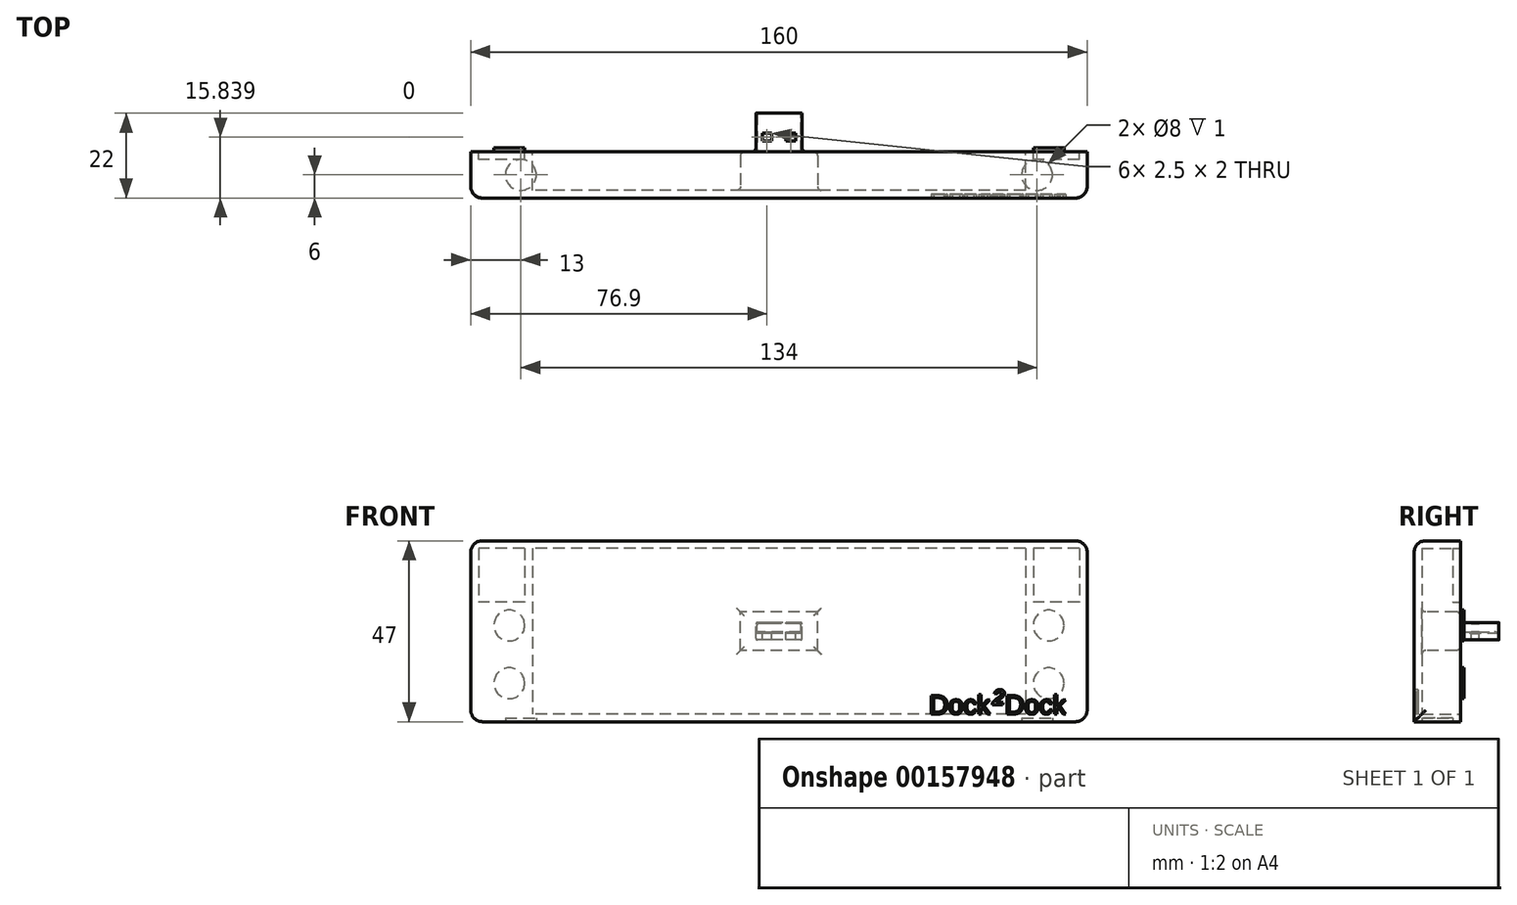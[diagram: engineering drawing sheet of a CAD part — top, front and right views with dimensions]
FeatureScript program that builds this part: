
annotation { "Feature Type Name" : "Feature", "Feature Type Description" : "" }
export const myFeature = defineFeature(function(context is Context, id is Id, definition is map)
    precondition{}
    {
        {
            var Q0;
            Q0=qCreatedBy(makeId("Right.planeOp"),FACE);
            var sketch = newSketch(context, id + "F0", { "sketchPlane" : qUnion([Q0])});
            skLineSegment(sketch, "E0.top", {"start": v(-6, -23.5) * mm, "end": v(6, -23.5) * mm});
            skLineSegment(sketch, "E0.left", {"start": v(-6, 23.5) * mm, "end": v(-6, -23.5) * mm});
            skLineSegment(sketch, "E0.right", {"start": v(6, 23.5) * mm, "end": v(6, -23.5) * mm});
            skPoint(sketch, "E0.middle", {"position": v(0, 0) * mm});
            skLineSegment(sketch, "E1.bottom", {"start": v(-6, 23.5) * mm, "end": v(6, 23.5) * mm});
            skLineSegment(sketch, "E1.left", {"start": v(-6, 23.5) * mm, "end": v(-6, 19.5) * mm});
            skLineSegment(sketch, "E1.right", {"start": v(6, 23.5) * mm, "end": v(6, 19.5) * mm});
            skSolve(sketch);
        }
        {
            var Q0;
            {var subQ1=sQuery(id+"F0.wireOp",EDGE,"E0.top");Q0=makeQuery(id+"F0.imprint","IMPRINT",FACE,{"disambiguationData":[TD([[makeQuery(id+"F0.imprint","IMPRINT",EDGE,{"derivedFrom":subQ1}),1.0]])]});}
            var Q1;
            {var subQ1=sQuery(id+"F0.wireOp",EDGE,"E0.top");Q1=makeQuery(id+"F0.imprint","IMPRINT",FACE,{"disambiguationData":[TD([[makeQuery(id+"F0.imprint","IMPRINT",EDGE,{"derivedFrom":subQ1}),1.0]])]});}
            extrude(context, id + "F1", {"entities" : qUnion([Q0, Q1]), "endBound" : BoundingType.SYMMETRIC, "depth" : 160 * mm});
        }
        {
            var Q0;
            Q0=makeQuery(id+"F1.opExtrude","SWEPT_FACE",FACE,{"disambiguationData":[OSD([sQuery(id+"F0.wireOp",EDGE,"E0.right")])]});
            var sketch = newSketch(context, id + "F2", { "sketchPlane" : qUnion([Q0])});
            skPoint(sketch, "E2.middle", {"position": v(0, 0) * mm});
            skLineSegment(sketch, "E3.bottom", {"start": v(70, 1.5) * mm, "end": v(-70, 1.5) * mm});
            skLineSegment(sketch, "E3.top", {"start": v(70, -13.5) * mm, "end": v(-70, -13.5) * mm});
            skLineSegment(sketch, "E3.left", {"start": v(70, 1.5) * mm, "end": v(70, -13.5) * mm});
            skLineSegment(sketch, "E3.right", {"start": v(-70, 1.5) * mm, "end": v(-70, -13.5) * mm});
            skCircle(sketch, "E4", {"center": v(70, 1.5) * mm, "radius": 4 * mm});
            skCircle(sketch, "E5", {"center": v(-70, 1.5) * mm, "radius": 4 * mm});
            skCircle(sketch, "E6", {"center": v(70, -13.5) * mm, "radius": 4 * mm});
            skCircle(sketch, "E7", {"center": v(-70, -13.5) * mm, "radius": 4 * mm});
            skSolve(sketch);
        }
        {
            var Q0;
            {var subQ0=sQuery(id+"F2.wireOp",EDGE,"E3.right");var subQ1=sQuery(id+"F2.wireOp",EDGE,"E3.top");var subQ2=makeQuery(id+"F2.imprint","INTERSECT",VERTEX,{"derivedFrom":[subQ1,subQ0]});Q0=makeQuery(id+"F2.imprint","IMPRINT",FACE,{"disambiguationData":[TD([[makeQuery(id+"F2.imprint","IMPRINT",EDGE,{"disambiguationData":[TD([[subQ2,1.0]])],"derivedFrom":subQ1}),1.0]])]});}
            var Q1;
            {var subQ0=sQuery(id+"F2.wireOp",EDGE,"E3.right");var subQ1=sQuery(id+"F2.wireOp",EDGE,"E3.top");var subQ2=makeQuery(id+"F2.imprint","INTERSECT",VERTEX,{"derivedFrom":[subQ1,subQ0]});Q1=makeQuery(id+"F2.imprint","IMPRINT",FACE,{"disambiguationData":[TD([[makeQuery(id+"F2.imprint","IMPRINT",EDGE,{"disambiguationData":[TD([[subQ2,1.0]])],"derivedFrom":subQ1}),-1.0]])]});}
            var Q2;
            {var subQ0=sQuery(id+"F2.wireOp",EDGE,"E3.right");var subQ1=sQuery(id+"F2.wireOp",EDGE,"E3.bottom");var subQ2=makeQuery(id+"F2.imprint","INTERSECT",VERTEX,{"derivedFrom":[subQ1,subQ0]});Q2=makeQuery(id+"F2.imprint","IMPRINT",FACE,{"disambiguationData":[TD([[makeQuery(id+"F2.imprint","IMPRINT",EDGE,{"disambiguationData":[TD([[subQ2,1.0]])],"derivedFrom":subQ1}),1.0]])]});}
            var Q3;
            {var subQ0=sQuery(id+"F2.wireOp",EDGE,"E3.right");var subQ1=sQuery(id+"F2.wireOp",EDGE,"E3.bottom");var subQ2=makeQuery(id+"F2.imprint","INTERSECT",VERTEX,{"derivedFrom":[subQ1,subQ0]});Q3=makeQuery(id+"F2.imprint","IMPRINT",FACE,{"disambiguationData":[TD([[makeQuery(id+"F2.imprint","IMPRINT",EDGE,{"disambiguationData":[TD([[subQ2,1.0]])],"derivedFrom":subQ1}),-1.0]])]});}
            var Q4;
            {var subQ0=sQuery(id+"F2.wireOp",EDGE,"E3.left");var subQ1=sQuery(id+"F2.wireOp",EDGE,"E3.top");var subQ2=makeQuery(id+"F2.imprint","INTERSECT",VERTEX,{"derivedFrom":[subQ1,subQ0]});Q4=makeQuery(id+"F2.imprint","IMPRINT",FACE,{"disambiguationData":[TD([[makeQuery(id+"F2.imprint","IMPRINT",EDGE,{"disambiguationData":[TD([[subQ2,-1.0]])],"derivedFrom":subQ1}),-1.0]])]});}
            var Q5;
            {var subQ0=sQuery(id+"F2.wireOp",EDGE,"E3.left");var subQ1=sQuery(id+"F2.wireOp",EDGE,"E3.top");var subQ2=makeQuery(id+"F2.imprint","INTERSECT",VERTEX,{"derivedFrom":[subQ1,subQ0]});Q5=makeQuery(id+"F2.imprint","IMPRINT",FACE,{"disambiguationData":[TD([[makeQuery(id+"F2.imprint","IMPRINT",EDGE,{"disambiguationData":[TD([[subQ2,-1.0]])],"derivedFrom":subQ1}),1.0]])]});}
            var Q6;
            {var subQ0=sQuery(id+"F2.wireOp",EDGE,"E3.left");var subQ1=sQuery(id+"F2.wireOp",EDGE,"E3.bottom");var subQ2=makeQuery(id+"F2.imprint","INTERSECT",VERTEX,{"derivedFrom":[subQ1,subQ0]});Q6=makeQuery(id+"F2.imprint","IMPRINT",FACE,{"disambiguationData":[TD([[makeQuery(id+"F2.imprint","IMPRINT",EDGE,{"disambiguationData":[TD([[subQ2,-1.0]])],"derivedFrom":subQ1}),-1.0]])]});}
            var Q7;
            {var subQ0=sQuery(id+"F2.wireOp",EDGE,"E3.left");var subQ1=sQuery(id+"F2.wireOp",EDGE,"E3.bottom");var subQ2=makeQuery(id+"F2.imprint","INTERSECT",VERTEX,{"derivedFrom":[subQ1,subQ0]});Q7=makeQuery(id+"F2.imprint","IMPRINT",FACE,{"disambiguationData":[TD([[makeQuery(id+"F2.imprint","IMPRINT",EDGE,{"disambiguationData":[TD([[subQ2,-1.0]])],"derivedFrom":subQ1}),1.0]])]});}
            var Q8;
            Q8=sQuery(id+"F2.wireOp",EDGE,"E5");
            extrude(context, id + "F3", {"entities" : qUnion([Q0, Q1, Q2, Q3, Q4, Q5, Q6, Q7]), "operationType" : NewBodyOperationType.ADD, "surfaceEntities" : qUnion([Q8]), "depth" : 1 * mm});
        }
        {
            var Q0;
            {var subQ0=sQuery(id+"F0.wireOp",EDGE,"E0.right");Q0=makeQuery(id+"F2.imprint","IMPRINT",FACE,{"disambiguationData":[TD([[makeQuery(id+"F2.imprint","IMPRINT",EDGE,{"derivedFrom":makeQuery(id+"F1.opExtrude","CAP_EDGE",EDGE,{"disambiguationData":[OSD([subQ0])],"isStart":true})}),-1.0]])]});}
            var sketch = newSketch(context, id + "F4", { "sketchPlane" : qUnion([Q0])});
            skLineSegment(sketch, "E8.bottom", {"start": v(-64, 21.5) * mm, "end": v(64, 21.5) * mm});
            skLineSegment(sketch, "E8.top", {"start": v(-64, -21.5) * mm, "end": v(64, -21.5) * mm});
            skLineSegment(sketch, "E8.left", {"start": v(-64, 21.5) * mm, "end": v(-64, -21.5) * mm});
            skLineSegment(sketch, "E8.right", {"start": v(64, 21.5) * mm, "end": v(64, -21.5) * mm});
            skPoint(sketch, "E8.middle", {"position": v(0, 0) * mm});
            skSolve(sketch);
        }
        {
            var Q0;
            Q0=qSketchRegion(id+"F4",true);
            extrude(context, id + "F5", {"entities" : qUnion([Q0]), "operationType" : NewBodyOperationType.REMOVE, "oppositeDirection" : true, "depth" : 10 * mm});
        }
        {
            var Q0;
            Q0=makeQuery(id+"F1.opExtrude","SWEPT_FACE",FACE,{"disambiguationData":[OSD([sQuery(id+"F0.wireOp",EDGE,"E0.top")])]});
            var sketch = newSketch(context, id + "F6", { "sketchPlane" : qUnion([Q0])});
            skCircle(sketch, "E9", {"center": v(67, 0) * mm, "radius": 4 * mm});
            skCircle(sketch, "E10", {"center": v(-67, 0) * mm, "radius": 4 * mm});
            skSolve(sketch);
        }
        {
            var Q0;
            Q0=qSketchRegion(id+"F6",true);
            extrude(context, id + "F7", {"entities" : qUnion([Q0]), "operationType" : NewBodyOperationType.REMOVE, "oppositeDirection" : true, "depth" : 1 * mm});
        }
        {
            var Q0;
            Q0=makeQuery(id+"F1.opExtrude","SWEPT_EDGE",EDGE,{"disambiguationData":[OSD([sQuery(id+"F0.wireOp",EDGE,"E0.left"),sQuery(id+"F0.wireOp",EDGE,"E1.bottom")])]});
            fillet(context, id + "F8", {"entities" : qUnion([Q0]), "radius" : 3 * mm, "tangentPropagation" : true, "allowEdgeOverflow" : false});
        }
        {
            var Q0;
            Q0=makeQuery(id+"F1.opExtrude","SWEPT_FACE",FACE,{"disambiguationData":[OSD([sQuery(id+"F0.wireOp",EDGE,"E0.left")])]});
            var sketch = newSketch(context, id + "F9", { "sketchPlane" : qUnion([Q0])});
            skText(sketch, "E11", { "text": "Dock  Dock", "fontName": "Arimo-Regular.ttf"});
            skText(sketch, "E12", { "text": "2", "fontName": "Arimo-BoldItalic.ttf"});
            const initialGuessF9  = {"E11": [0.039, -0.0215, 1, 0, 0.005], "E12": [0.05543, -0.01913, 1, 0, 0.0041]};
            skSetInitialGuess(sketch, initialGuessF9);
            skSolve(sketch);
        }
        {
            var Q0;
            Q0=qSketchRegion(id+"F9",true);
            extrude(context, id + "F10", {"entities" : qUnion([Q0]), "operationType" : NewBodyOperationType.REMOVE, "oppositeDirection" : true, "depth" : 1 * mm});
        }
        {
            var Q0;
            Q0=makeQuery(id+"F1.opExtrude","CAP_EDGE",EDGE,{"disambiguationData":[OSD([sQuery(id+"F0.wireOp",EDGE,"E1.bottom")])],"isStart":true});
            var Q1;
            {var subQ0=sQuery(id+"F0.wireOp",EDGE,"E1.bottom");var subQ1=sQuery(id+"F0.wireOp",EDGE,"E0.left");Q1=makeQuery(id+"F8.opFillet","BLEND_EDGE",EDGE,{"blendedFrom":[makeQuery(id+"F1.opExtrude","SWEPT_EDGE",EDGE,{"disambiguationData":[OSD([subQ1,subQ0])]}),makeQuery(id+"F1.opExtrude","CAP_FACE",FACE,{"disambiguationData":[OSD([sQuery(id+"F0.wireOp",EDGE,"E0.top"),subQ1,sQuery(id+"F0.wireOp",EDGE,"E0.right"),subQ0])],"isStart":true})],"blendedInto":[makeQuery(id+"F1.opExtrude","CAP_FACE",FACE,{"disambiguationData":[OSD([sQuery(id+"F0.wireOp",EDGE,"E0.top"),subQ1,sQuery(id+"F0.wireOp",EDGE,"E0.right"),subQ0])],"isStart":true})]});}
            var Q2;
            Q2=makeQuery(id+"F1.opExtrude","CAP_EDGE",EDGE,{"disambiguationData":[OSD([sQuery(id+"F0.wireOp",EDGE,"E0.left")])],"isStart":true});
            var Q3;
            Q3=makeQuery(id+"F1.opExtrude","CAP_EDGE",EDGE,{"disambiguationData":[OSD([sQuery(id+"F0.wireOp",EDGE,"E0.left")])],"isStart":false});
            var Q4;
            {var subQ0=sQuery(id+"F0.wireOp",EDGE,"E1.bottom");var subQ1=sQuery(id+"F0.wireOp",EDGE,"E0.left");Q4=makeQuery(id+"F8.opFillet","BLEND_EDGE",EDGE,{"blendedFrom":[makeQuery(id+"F1.opExtrude","SWEPT_EDGE",EDGE,{"disambiguationData":[OSD([subQ1,subQ0])]}),makeQuery(id+"F1.opExtrude","CAP_FACE",FACE,{"disambiguationData":[OSD([sQuery(id+"F0.wireOp",EDGE,"E0.top"),subQ1,sQuery(id+"F0.wireOp",EDGE,"E0.right"),subQ0])],"isStart":false})],"blendedInto":[makeQuery(id+"F1.opExtrude","CAP_FACE",FACE,{"disambiguationData":[OSD([sQuery(id+"F0.wireOp",EDGE,"E0.top"),subQ1,sQuery(id+"F0.wireOp",EDGE,"E0.right"),subQ0])],"isStart":false})]});}
            var Q5;
            Q5=makeQuery(id+"F1.opExtrude","CAP_EDGE",EDGE,{"disambiguationData":[OSD([sQuery(id+"F0.wireOp",EDGE,"E1.bottom")])],"isStart":false});
            var Q6;
            Q6=makeQuery(id+"F1.opExtrude","CAP_EDGE",EDGE,{"disambiguationData":[OSD([sQuery(id+"F0.wireOp",EDGE,"E0.top")])],"isStart":false});
            var Q7;
            Q7=makeQuery(id+"F1.opExtrude","CAP_EDGE",EDGE,{"disambiguationData":[OSD([sQuery(id+"F0.wireOp",EDGE,"E0.top")])],"isStart":true});
            fillet(context, id + "F11", {"entities" : qUnion([Q0, Q1, Q2, Q3, Q4, Q5, Q6, Q7]), "radius" : 3 * mm, "tangentPropagation" : true, "allowEdgeOverflow" : false});
        }
        {
            var Q0;
            {var subQ0=sQuery(id+"F0.wireOp",EDGE,"E0.right");Q0=makeQuery(id+"F2.imprint","IMPRINT",FACE,{"disambiguationData":[TD([[makeQuery(id+"F2.imprint","IMPRINT",EDGE,{"derivedFrom":makeQuery(id+"F1.opExtrude","CAP_EDGE",EDGE,{"disambiguationData":[OSD([subQ0])],"isStart":true})}),-1.0]])]});}
            var sketch = newSketch(context, id + "F12", { "sketchPlane" : qUnion([Q0])});
            skLineSegment(sketch, "E13.bottom", {"start": v(-78, 21.5) * mm, "end": v(-66, 21.5) * mm});
            skLineSegment(sketch, "E13.top", {"start": v(-78, 7.5) * mm, "end": v(-66, 7.5) * mm});
            skLineSegment(sketch, "E13.left", {"start": v(-78, 21.5) * mm, "end": v(-78, 7.5) * mm});
            skLineSegment(sketch, "E13.right", {"start": v(-66, 21.5) * mm, "end": v(-66, 7.5) * mm});
            skLineSegment(sketch, "E14.bottom", {"start": v(66, 21.5) * mm, "end": v(78, 21.5) * mm});
            skLineSegment(sketch, "E14.top", {"start": v(66, 7.5) * mm, "end": v(78, 7.5) * mm});
            skLineSegment(sketch, "E14.left", {"start": v(66, 21.5) * mm, "end": v(66, 7.5) * mm});
            skLineSegment(sketch, "E14.right", {"start": v(78, 21.5) * mm, "end": v(78, 7.5) * mm});
            skSolve(sketch);
        }
        {
            var Q0;
            Q0=qSketchRegion(id+"F12",true);
            extrude(context, id + "F13", {"entities" : qUnion([Q0]), "operationType" : NewBodyOperationType.REMOVE, "oppositeDirection" : true, "depth" : 2 * mm});
        }
        {
            var Q0;
            {var subQ2=sQuery(id+"F0.wireOp",EDGE,"E0.left");var subQ3=sQuery(id+"F0.wireOp",EDGE,"E0.top");Q0=makeQuery(id+"F10.boolean.opBoolean","SPLIT",FACE,{"disambiguationData":[TD([makeQuery(id+"F1.opExtrude","SWEPT_FACE",FACE,{"disambiguationData":[OSD([subQ3])]})])],"derivedFrom":makeQuery(id+"F1.opExtrude","SWEPT_FACE",FACE,{"disambiguationData":[OSD([subQ2])]})});}
            var sketch = newSketch(context, id + "F14", { "sketchPlane" : qUnion([Q0])});
            skLineSegment(sketch, "E15.bottom", {"start": v(-10, 5) * mm, "end": v(10, 5) * mm});
            skLineSegment(sketch, "E15.top", {"start": v(-10, -5) * mm, "end": v(10, -5) * mm});
            skLineSegment(sketch, "E15.left", {"start": v(-10, 5) * mm, "end": v(-10, -5) * mm});
            skLineSegment(sketch, "E15.right", {"start": v(10, 5) * mm, "end": v(10, -5) * mm});
            skSolve(sketch);
        }
        {
            var Q0;
            Q0=qSketchRegion(id+"F14",true);
            extrude(context, id + "F15", {"entities" : qUnion([Q0]), "operationType" : NewBodyOperationType.ADD, "oppositeDirection" : true, "depth" : 12 * mm});
        }
        {
            var Q0;
            Q0=makeQuery(id+"F15.opExtrude","CAP_FACE",FACE,{"disambiguationData":[OSD([sQuery(id+"F14.wireOp",EDGE,"E15.bottom"),sQuery(id+"F14.wireOp",EDGE,"E15.top"),sQuery(id+"F14.wireOp",EDGE,"E15.left"),sQuery(id+"F14.wireOp",EDGE,"E15.right")])],"isStart":false});
            var sketch = newSketch(context, id + "F16", { "sketchPlane" : qUnion([Q0])});
            skLineSegment(sketch, "E16.bottom", {"start": v(-6, -2.25) * mm, "end": v(6, -2.25) * mm});
            skLineSegment(sketch, "E16.top", {"start": v(-6, 2.25) * mm, "end": v(6, 2.25) * mm});
            skLineSegment(sketch, "E16.left", {"start": v(-6, -2.25) * mm, "end": v(-6, 2.25) * mm});
            skLineSegment(sketch, "E16.right", {"start": v(6, -2.25) * mm, "end": v(6, 2.25) * mm});
            skPoint(sketch, "E16.middle", {"position": v(0, 0) * mm});
            skLineSegment(sketch, "E17.bottom", {"start": v(-5.7, -0.6) * mm, "end": v(5.7, -0.6) * mm});
            skLineSegment(sketch, "E17.top", {"start": v(-5.7, 1.95) * mm, "end": v(5.7, 1.95) * mm});
            skLineSegment(sketch, "E17.left", {"start": v(-5.7, -0.6) * mm, "end": v(-5.7, 1.95) * mm});
            skLineSegment(sketch, "E17.right", {"start": v(5.7, -0.6) * mm, "end": v(5.7, 1.95) * mm});
            skSolve(sketch);
        }
        {
            var Q0;
            Q0=qSketchRegion(id+"F16",true);
            extrude(context, id + "F17", {"entities" : qUnion([Q0]), "operationType" : NewBodyOperationType.ADD, "depth" : 10 * mm});
        }
        {
            var Q0;
            Q0=makeQuery(id+"F17.opExtrude","SWEPT_EDGE",EDGE,{"disambiguationData":[OSD([sQuery(id+"F16.wireOp",EDGE,"E17.top"),sQuery(id+"F16.wireOp",EDGE,"E17.left")])]});
            var Q1;
            Q1=makeQuery(id+"F17.opExtrude","SWEPT_EDGE",EDGE,{"disambiguationData":[OSD([sQuery(id+"F16.wireOp",EDGE,"E17.top"),sQuery(id+"F16.wireOp",EDGE,"E17.right")])]});
            var Q2;
            Q2=makeQuery(id+"F17.opExtrude","SWEPT_EDGE",EDGE,{"disambiguationData":[OSD([sQuery(id+"F16.wireOp",EDGE,"E16.top"),sQuery(id+"F16.wireOp",EDGE,"E16.left")])]});
            var Q3;
            Q3=makeQuery(id+"F17.opExtrude","SWEPT_EDGE",EDGE,{"disambiguationData":[OSD([sQuery(id+"F16.wireOp",EDGE,"E16.bottom"),sQuery(id+"F16.wireOp",EDGE,"E16.left")])]});
            var Q4;
            Q4=makeQuery(id+"F17.opExtrude","SWEPT_EDGE",EDGE,{"disambiguationData":[OSD([sQuery(id+"F16.wireOp",EDGE,"E16.bottom"),sQuery(id+"F16.wireOp",EDGE,"E16.right")])]});
            var Q5;
            Q5=makeQuery(id+"F17.opExtrude","SWEPT_EDGE",EDGE,{"disambiguationData":[OSD([sQuery(id+"F16.wireOp",EDGE,"E16.top"),sQuery(id+"F16.wireOp",EDGE,"E16.right")])]});
            fillet(context, id + "F18", {"entities" : qUnion([Q0, Q1, Q2, Q3, Q4, Q5]), "radius" : 0.4 * mm, "tangentPropagation" : true, "allowEdgeOverflow" : false});
        }
        {
            var Q0;
            Q0=makeQuery(id+"F17.opExtrude","CAP_FACE",FACE,{"disambiguationData":[OSD([sQuery(id+"F16.wireOp",EDGE,"E16.bottom"),sQuery(id+"F16.wireOp",EDGE,"E16.top"),sQuery(id+"F16.wireOp",EDGE,"E16.left"),sQuery(id+"F16.wireOp",EDGE,"E16.right"),sQuery(id+"F16.wireOp",EDGE,"E17.bottom"),sQuery(id+"F16.wireOp",EDGE,"E17.top"),sQuery(id+"F16.wireOp",EDGE,"E17.left"),sQuery(id+"F16.wireOp",EDGE,"E17.right")])],"isStart":false});
            var sketch = newSketch(context, id + "F19", { "sketchPlane" : qUnion([Q0])});
            skLineSegment(sketch, "E18.bottom", {"start": v(-5.7, -0.6) * mm, "end": v(5.7, -0.6) * mm});
            skLineSegment(sketch, "E18.top", {"start": v(-5.7, -0.2) * mm, "end": v(5.7, -0.2) * mm});
            skLineSegment(sketch, "E18.left", {"start": v(-5.7, -0.6) * mm, "end": v(-5.7, -0.2) * mm});
            skLineSegment(sketch, "E18.right", {"start": v(5.7, -0.6) * mm, "end": v(5.7, -0.2) * mm});
            skSolve(sketch);
        }
        {
            var Q0;
            Q0=qSketchRegion(id+"F19",true);
            extrude(context, id + "F20", {"entities" : qUnion([Q0]), "oppositeDirection" : true, "depth" : 10 * mm});
        }
        {
            var Q0;
            Q0=makeQuery(id+"F20.opExtrude","CAP_EDGE",EDGE,{"disambiguationData":[OSD([sQuery(id+"F19.wireOp",EDGE,"E18.top")])],"isStart":true});
            fillet(context, id + "F21", {"entities" : qUnion([Q0]), "radius" : 2 * mm, "tangentPropagation" : true, "allowEdgeOverflow" : false});
        }
        {
            var Q0;
            Q0=makeQuery(id+"F17.opExtrude","SWEPT_FACE",FACE,{"disambiguationData":[OSD([sQuery(id+"F16.wireOp",EDGE,"E16.top")])]});
            var sketch = newSketch(context, id + "F22", { "sketchPlane" : qUnion([Q0])});
            skLineSegment(sketch, "E19.bottom", {"start": v(4.35, 8.84) * mm, "end": v(1.85, 8.84) * mm});
            skLineSegment(sketch, "E19.top", {"start": v(4.35, 10.84) * mm, "end": v(1.85, 10.84) * mm});
            skLineSegment(sketch, "E19.left", {"start": v(4.35, 8.84) * mm, "end": v(4.35, 10.84) * mm});
            skLineSegment(sketch, "E19.right", {"start": v(1.85, 8.84) * mm, "end": v(1.85, 10.84) * mm});
            skLineSegment(sketch, "E20.bottom", {"start": v(-1.85, 8.84) * mm, "end": v(-4.35, 8.84) * mm});
            skLineSegment(sketch, "E20.top", {"start": v(-1.85, 10.84) * mm, "end": v(-4.35, 10.84) * mm});
            skLineSegment(sketch, "E20.left", {"start": v(-1.85, 8.84) * mm, "end": v(-1.85, 10.84) * mm});
            skLineSegment(sketch, "E20.right", {"start": v(-4.35, 8.84) * mm, "end": v(-4.35, 10.84) * mm});
            skSolve(sketch);
        }
        {
            var Q0;
            Q0=qSketchRegion(id+"F22",true);
            extrude(context, id + "F23", {"entities" : qUnion([Q0]), "operationType" : NewBodyOperationType.REMOVE, "oppositeDirection" : true, "depth" : 5 * mm});
        }
        {
            var Q0;
            {var subQ0=sQuery(id+"F14.wireOp",EDGE,"E15.left");var subQ1=sQuery(id+"F14.wireOp",EDGE,"E15.top");var subQ2=sQuery(id+"F14.wireOp",EDGE,"E15.right");var subQ3=sQuery(id+"F14.wireOp",EDGE,"E15.bottom");Q0=makeQuery(id+"F17.boolean.opBoolean","SPLIT",FACE,{"disambiguationData":[TD([makeQuery(id+"F15.opExtrude","SWEPT_FACE",FACE,{"disambiguationData":[OSD([subQ3])]})])],"derivedFrom":makeQuery(id+"F15.opExtrude","CAP_FACE",FACE,{"disambiguationData":[OSD([subQ3,subQ1,subQ0,subQ2])],"isStart":false})});}
            var Q1;
            Q1=makeQuery(id+"F15.boolean.opBoolean","INTERSECT",EDGE,{"derivedFrom":[makeQuery(id+"F5.boolean.opBoolean","COPY",FACE,{"derivedFrom":makeQuery(id+"F5.opExtrude","CAP_FACE",FACE,{"disambiguationData":[OSD([sQuery(id+"F4.wireOp",EDGE,"E8.bottom"),sQuery(id+"F4.wireOp",EDGE,"E8.top"),sQuery(id+"F4.wireOp",EDGE,"E8.left"),sQuery(id+"F4.wireOp",EDGE,"E8.right")])],"isStart":false})}),makeQuery(id+"F15.opExtrude","SWEPT_FACE",FACE,{"disambiguationData":[OSD([sQuery(id+"F14.wireOp",EDGE,"E15.bottom")])]})]});
            var Q2;
            Q2=makeQuery(id+"F15.boolean.opBoolean","INTERSECT",EDGE,{"derivedFrom":[makeQuery(id+"F5.boolean.opBoolean","COPY",FACE,{"derivedFrom":makeQuery(id+"F5.opExtrude","CAP_FACE",FACE,{"disambiguationData":[OSD([sQuery(id+"F4.wireOp",EDGE,"E8.bottom"),sQuery(id+"F4.wireOp",EDGE,"E8.top"),sQuery(id+"F4.wireOp",EDGE,"E8.left"),sQuery(id+"F4.wireOp",EDGE,"E8.right")])],"isStart":false})}),makeQuery(id+"F15.opExtrude","SWEPT_FACE",FACE,{"disambiguationData":[OSD([sQuery(id+"F14.wireOp",EDGE,"E15.left")])]})]});
            var Q3;
            Q3=makeQuery(id+"F15.boolean.opBoolean","INTERSECT",EDGE,{"derivedFrom":[makeQuery(id+"F5.boolean.opBoolean","COPY",FACE,{"derivedFrom":makeQuery(id+"F5.opExtrude","CAP_FACE",FACE,{"disambiguationData":[OSD([sQuery(id+"F4.wireOp",EDGE,"E8.bottom"),sQuery(id+"F4.wireOp",EDGE,"E8.top"),sQuery(id+"F4.wireOp",EDGE,"E8.left"),sQuery(id+"F4.wireOp",EDGE,"E8.right")])],"isStart":false})}),makeQuery(id+"F15.opExtrude","SWEPT_FACE",FACE,{"disambiguationData":[OSD([sQuery(id+"F14.wireOp",EDGE,"E15.top")])]})]});
            var Q4;
            Q4=makeQuery(id+"F15.boolean.opBoolean","INTERSECT",EDGE,{"derivedFrom":[makeQuery(id+"F5.boolean.opBoolean","COPY",FACE,{"derivedFrom":makeQuery(id+"F5.opExtrude","CAP_FACE",FACE,{"disambiguationData":[OSD([sQuery(id+"F4.wireOp",EDGE,"E8.bottom"),sQuery(id+"F4.wireOp",EDGE,"E8.top"),sQuery(id+"F4.wireOp",EDGE,"E8.left"),sQuery(id+"F4.wireOp",EDGE,"E8.right")])],"isStart":false})}),makeQuery(id+"F15.opExtrude","SWEPT_FACE",FACE,{"disambiguationData":[OSD([sQuery(id+"F14.wireOp",EDGE,"E15.right")])]})]});
            fillet(context, id + "F24", {"entities" : qUnion([Q0, Q1, Q2, Q3, Q4]), "radius" : 1 * mm, "tangentPropagation" : true, "allowEdgeOverflow" : false});
        }
    });
